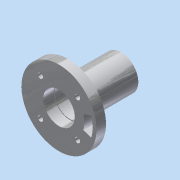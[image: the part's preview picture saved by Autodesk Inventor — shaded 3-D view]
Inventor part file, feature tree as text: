
AUTODESK INVENTOR PART (.ipt)
format: ipt  version: 2015 (Build 190159000, 159)  size: 138,240 bytes
history: native  units: in
note: dims shown in document units (in); Inventor stores cm internally (conversion verified against a paired STEP export)
features: sketch x2, other x1, revolve x1, extrude x1
ambient origin geometry x8: Origin, YZ Plane, XZ Plane, XY Plane, X Axis, Y Axis, Z Axis, Center Point
bodies: Solid1 (feature_tree)
feature tree (5):
  other  "Stator.ipt"
  sketch  "Sketch1"  dims[d0=0.9843in d1=0.25in]
  revolve  "Revolution1"  [1 undecoded]
  extrude  "Extrusion1"  Depth=1.378in
  sketch  "Sketch2"  dims[d3=0.3937in d4=1.378in d5=0.1575in d6=0.2825in d7=0.4134in d9=0.0197in d10=90.0deg d11=0.4528in d12=0.1378in d15=45.0deg d17=1.5748in d19=360.0deg d21=1.0in d22=0.0in]
note: 1 required parameter value undecoded (feature->parameter linkage not recoverable at this tier; creation-order binding heuristic only, values carry confidence <= 0.55)
